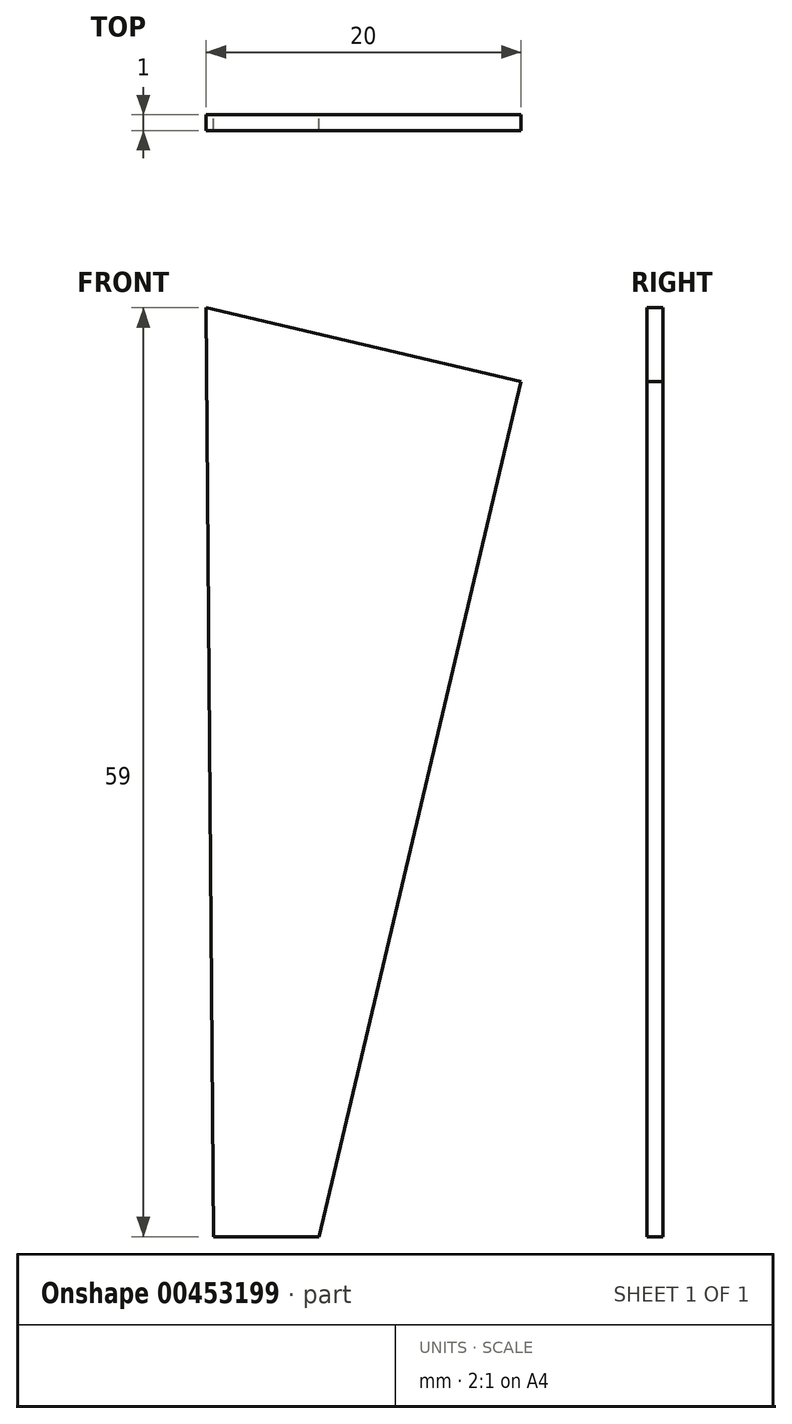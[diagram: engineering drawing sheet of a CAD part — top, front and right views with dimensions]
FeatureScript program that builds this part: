
annotation { "Feature Type Name" : "Feature", "Feature Type Description" : "" }
export const myFeature = defineFeature(function(context is Context, id is Id, definition is map)
    precondition{}
    {
        {
            var Q0;
            Q0=qCreatedBy(makeId("Front.planeOp"),FACE);
            var sketch = newSketch(context, id + "F0", { "sketchPlane" : qUnion([Q0])});
            skLineSegment(sketch, "E0", {"start": v(0.48, 0) * mm, "end": v(7.18, 0) * mm});
            skLineSegment(sketch, "E1", {"start": v(7.18, 0) * mm, "end": v(20, 54.3) * mm});
            skLineSegment(sketch, "E2", {"start": v(20, 54.3) * mm, "end": v(0, 59) * mm});
            skLineSegment(sketch, "E3", {"start": v(0, 59) * mm, "end": v(0.48, 0) * mm});
            skSolve(sketch);
        }
        {
            var Q0;
            Q0=qSketchRegion(id+"F0",true);
            extrude(context, id + "F1", {"entities" : qUnion([Q0]), "depth" : 1 * mm});
        }
    });
